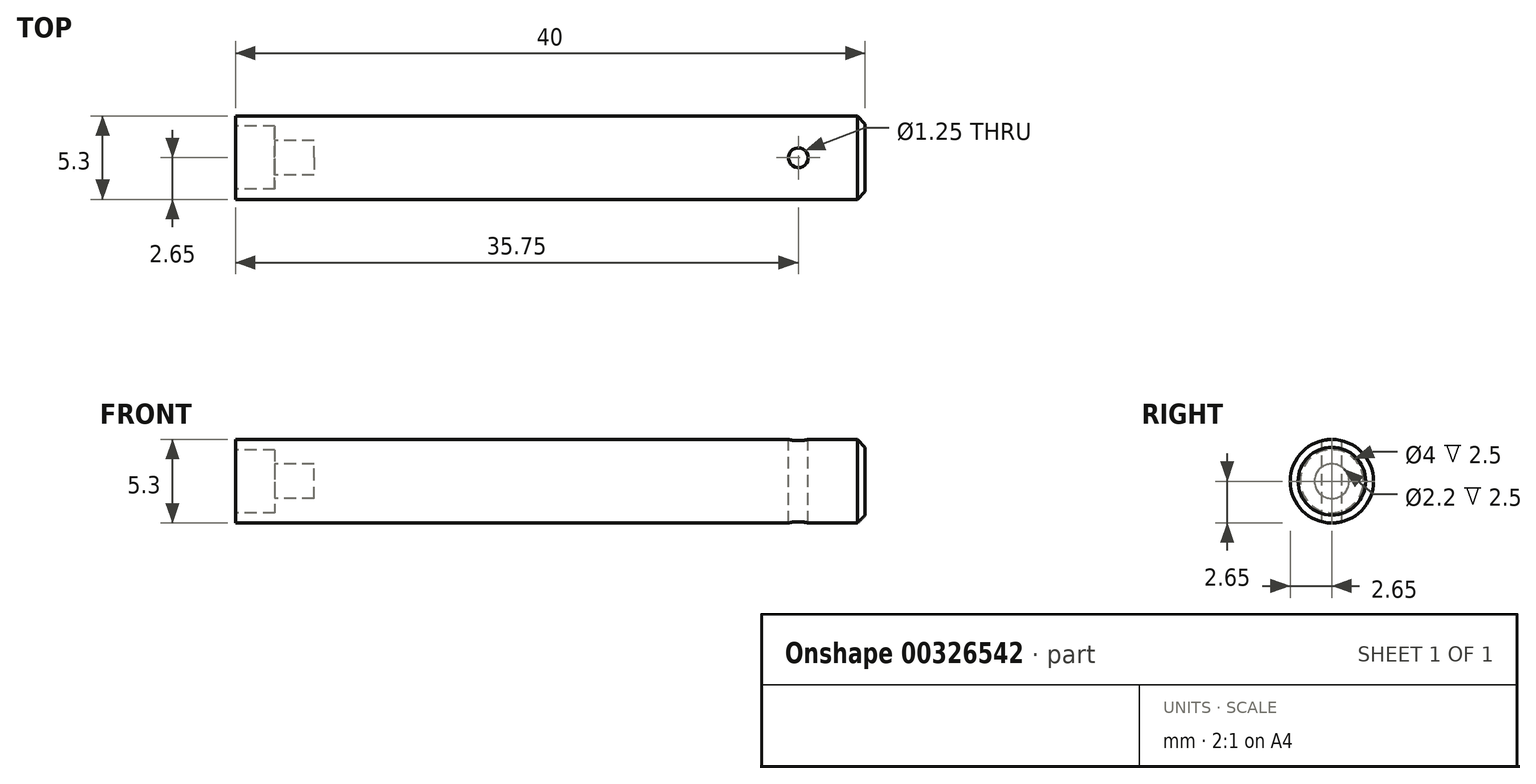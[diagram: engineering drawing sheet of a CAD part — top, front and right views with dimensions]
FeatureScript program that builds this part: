
annotation { "Feature Type Name" : "Feature", "Feature Type Description" : "" }
export const myFeature = defineFeature(function(context is Context, id is Id, definition is map)
    precondition{}
    {
        {
            var Q0;
            Q0=qCreatedBy(makeId("Right.planeOp"),FACE);
            var sketch = newSketch(context, id + "F0", { "sketchPlane" : qUnion([Q0])});
            skCircle(sketch, "E0", {"center": v(0, 0) * mm, "radius": 2.65 * mm});
            skSolve(sketch);
        }
        {
            var Q0;
            Q0=makeQuery(id+"F0.imprint","IMPRINT",FACE,{"disambiguationData":[TD([[makeQuery(id+"F0.imprint","IMPRINT",EDGE,{"derivedFrom":sQuery(id+"F0.wireOp",EDGE,"E0")}),1.0]])]});
            extrude(context, id + "F1", {"entities" : qUnion([Q0]), "depth" : 40 * mm});
        }
        {
            var Q0;
            Q0=qCreatedBy(makeId("Right.planeOp"),FACE);
            var sketch = newSketch(context, id + "F2", { "sketchPlane" : qUnion([Q0])});
            skCircle(sketch, "E1", {"center": v(0, 0) * mm, "radius": 1.1 * mm});
            skSolve(sketch);
        }
        {
            var Q0;
            Q0 = qSketchRegion(id + "F2", true);
            extrude(context, id + "F3", {"entities" : qUnion([Q0]), "operationType" : NewBodyOperationType.REMOVE, "depth" : 5 * mm});
        }
        {
            var Q0;
            Q0=makeQuery(id+"F1.opExtrude","CAP_EDGE",EDGE,{"disambiguationData":[OSD([sQuery(id+"F0.wireOp",EDGE,"E0")])],"isStart":false});
            chamfer(context, id + "F4", {"entities" : qUnion([Q0]), "width" : .5 * mm, "tangentPropagation" : true});
        }
        {
            var Q0;
            Q0=qCreatedBy(makeId("Top.planeOp"),FACE);
            var sketch = newSketch(context, id + "F5", { "sketchPlane" : qUnion([Q0])});
            skCircle(sketch, "E2", {"center": v(35.75, 0) * mm, "radius": 0.62 * mm});
            skSolve(sketch);
        }
        {
            var Q0;
            Q0 = qSketchRegion(id + "F5", true);
            extrude(context, id + "F6", {"entities" : qUnion([Q0]), "operationType" : NewBodyOperationType.REMOVE, "oppositeDirection" : true, "depth" : 25 * mm, "symmetric" : true});
        }
        {
            var Q0;
            Q0=makeQuery(id+"F1.opExtrude","CAP_FACE",FACE,{"disambiguationData":[OSD([sQuery(id+"F0.wireOp",EDGE,"E0")])],"isStart":true});
            var sketch = newSketch(context, id + "F7", { "sketchPlane" : qUnion([Q0])});
            skCircle(sketch, "E3", {"center": v(0, 0) * mm, "radius": 2 * mm});
            skSolve(sketch);
        }
        {
            var Q0;
            Q0 = qSketchRegion(id + "F7", true);
            extrude(context, id + "F8", {"entities" : qUnion([Q0]), "operationType" : NewBodyOperationType.REMOVE, "oppositeDirection" : true, "depth" : 2.5 * mm});
        }
    });
